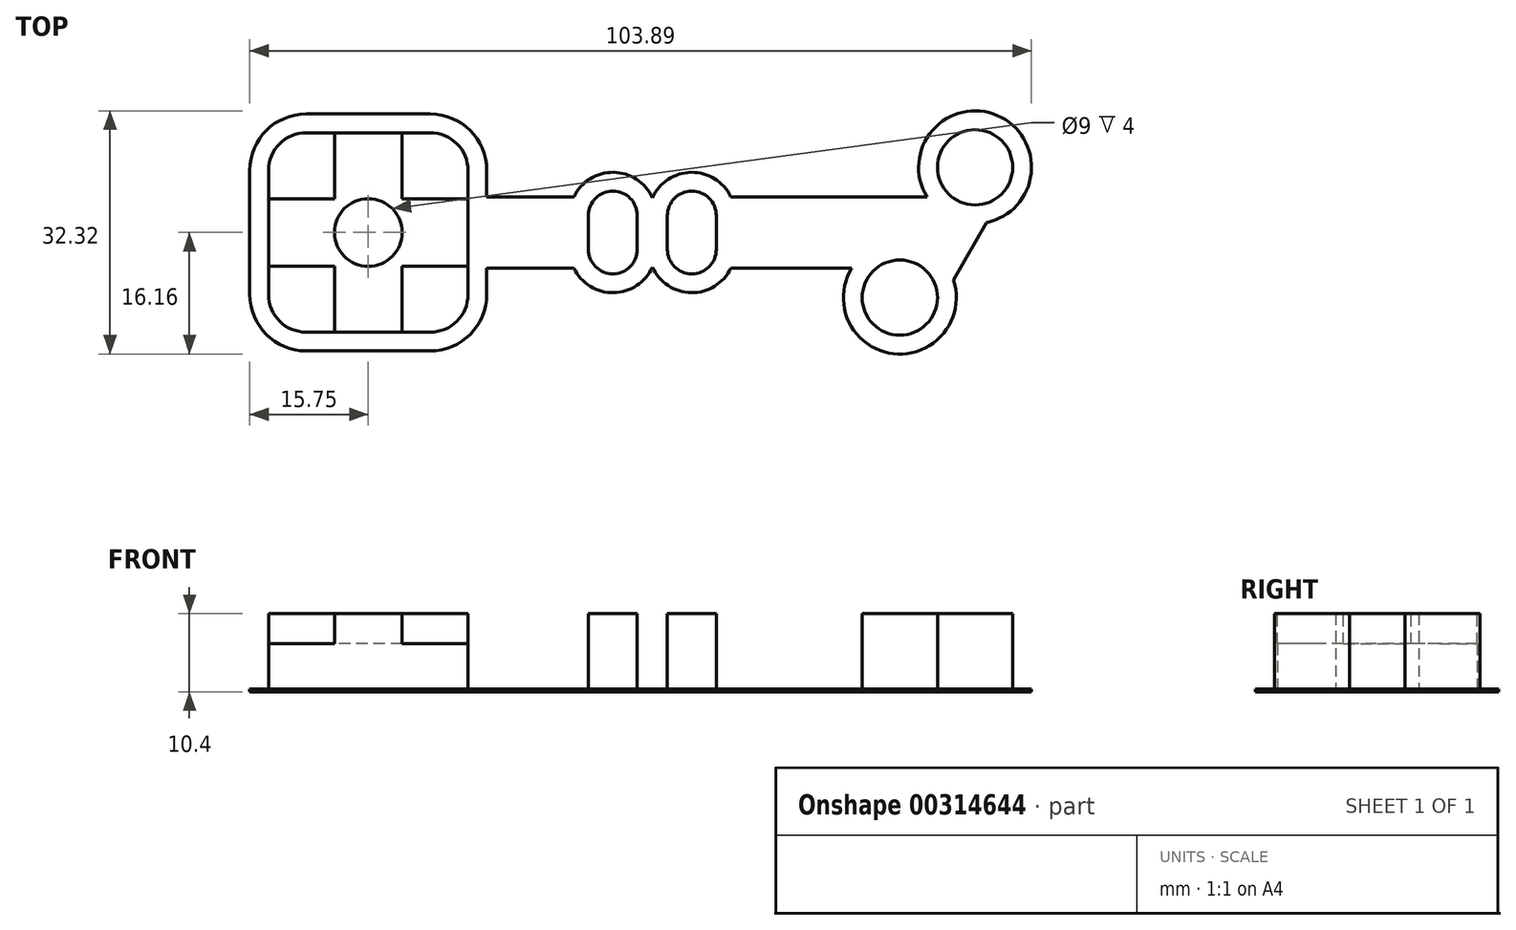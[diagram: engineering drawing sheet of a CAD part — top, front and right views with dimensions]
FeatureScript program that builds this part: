
annotation { "Feature Type Name" : "Feature", "Feature Type Description" : "" }
export const myFeature = defineFeature(function(context is Context, id is Id, definition is map)
    precondition{}
    {
        {
            var Q0;
            Q0=qCreatedBy(makeId("Top.planeOp"),FACE);
            var sketch = newSketch(context, id + "F0", { "sketchPlane" : qUnion([Q0])});
            skLineSegment(sketch, "E0.bottom", {"start": v(-8.25, 13.25) * mm, "end": v(8.25, 13.25) * mm});
            skLineSegment(sketch, "E0.top", {"start": v(-8.25, -13.25) * mm, "end": v(8.25, -13.25) * mm});
            skLineSegment(sketch, "E0.left", {"start": v(-13.25, 8.25) * mm, "end": v(-13.25, -8.25) * mm});
            skLineSegment(sketch, "E0.right", {"start": v(13.25, 8.25) * mm, "end": v(13.25, 2.25) * mm});
            skPoint(sketch, "E0.middle", {"position": v(0, 0) * mm});
            skPoint(sketch, "E1.visualSharp", {"position": v(-13.25, 13.25) * mm});
            skArc(sketch, "E1.filletArc", {"start": v(-8.25, 13.25) * mm, "mid": v(-11.79, 11.79) * mm, "end": v(-13.25, 8.25) * mm});
            skPoint(sketch, "E2.visualSharp", {"position": v(13.25, 13.25) * mm});
            skArc(sketch, "E2.filletArc", {"start": v(13.25, 8.25) * mm, "mid": v(11.79, 11.79) * mm, "end": v(8.25, 13.25) * mm});
            skPoint(sketch, "E3.visualSharp", {"position": v(13.25, -13.25) * mm});
            skArc(sketch, "E3.filletArc", {"start": v(8.25, -13.25) * mm, "mid": v(11.79, -11.79) * mm, "end": v(13.25, -8.25) * mm});
            skPoint(sketch, "E4.visualSharp", {"position": v(-13.25, -13.25) * mm});
            skArc(sketch, "E4.filletArc", {"start": v(-13.25, -8.25) * mm, "mid": v(-11.79, -11.79) * mm, "end": v(-8.25, -13.25) * mm});
            skCircle(sketch, "E5", {"center": v(0, 0) * mm, "radius": 4.5 * mm});
            skLineSegment(sketch, "E6", {"start": v(-4.5, 13.25) * mm, "end": v(-4.5, -13.25) * mm});
            skLineSegment(sketch, "E7", {"start": v(4.5, 13.25) * mm, "end": v(4.5, -13.25) * mm});
            skLineSegment(sketch, "E8", {"start": v(-13.25, 4.5) * mm, "end": v(13.25, 4.5) * mm});
            skLineSegment(sketch, "E9", {"start": v(-13.25, -4.5) * mm, "end": v(13.25, -4.5) * mm});
            skLineSegment(sketch, "E10", {"start": v(-52.76, 0) * mm, "end": v(91.1, 0) * mm, "construction": true});
            skLineSegment(sketch, "E11", {"start": v(13.25, 2.25) * mm, "end": v(29.25, 2.25) * mm});
            skLineSegment(sketch, "E12.bottom", {"start": v(29.25, 2.25) * mm, "end": v(35.75, 2.25) * mm});
            skLineSegment(sketch, "E12.top", {"start": v(29.25, -2.25) * mm, "end": v(35.75, -2.25) * mm});
            skLineSegment(sketch, "E12.left", {"start": v(29.25, 2.25) * mm, "end": v(29.25, -2.25) * mm});
            skLineSegment(sketch, "E12.right", {"start": v(35.75, 2.25) * mm, "end": v(35.75, -2.25) * mm});
            skLineSegment(sketch, "E13", {"start": v(37.75, 18.47) * mm, "end": v(37.75, -25.73) * mm, "construction": true});
            skLineSegment(sketch, "E14.MirrorCS", {"start": v(13.25, -2.25) * mm, "end": v(29.25, -2.25) * mm});
            skLineSegment(sketch, "E15.MirrorCS", {"start": v(46.25, 2.25) * mm, "end": v(46.25, -2.25) * mm});
            skLineSegment(sketch, "E16.MirrorCS", {"start": v(39.75, 2.25) * mm, "end": v(39.75, -2.25) * mm});
            skLineSegment(sketch, "E17.MirrorCS", {"start": v(46.25, -2.25) * mm, "end": v(39.75, -2.25) * mm});
            skLineSegment(sketch, "E18.MirrorCS", {"start": v(46.25, 2.25) * mm, "end": v(39.75, 2.25) * mm});
            skLineSegment(sketch, "E19", {"start": v(35.75, 2.25) * mm, "end": v(39.75, 2.25) * mm});
            skLineSegment(sketch, "E20", {"start": v(35.75, -2.25) * mm, "end": v(39.75, -2.25) * mm});
            skArc(sketch, "E21", {"start": v(29.25, 2.25) * mm, "mid": v(32.5, 5.5) * mm, "end": v(35.75, 2.25) * mm});
            skArc(sketch, "E22.MirrorCS", {"start": v(29.25, -2.25) * mm, "mid": v(32.5, -5.5) * mm, "end": v(35.75, -2.25) * mm});
            skArc(sketch, "E23.MirrorCS", {"start": v(46.25, 2.25) * mm, "mid": v(43, 5.5) * mm, "end": v(39.75, 2.25) * mm});
            skArc(sketch, "E24.MirrorCS", {"start": v(46.25, -2.25) * mm, "mid": v(43, -5.5) * mm, "end": v(39.75, -2.25) * mm});
            skLineSegment(sketch, "E25", {"start": v(46.25, 2.25) * mm, "end": v(74.05, 2.25) * mm});
            skLineSegment(sketch, "E26", {"start": v(80.64, 8.66) * mm, "end": v(70.64, -8.66) * mm, "construction": true});
            skPoint(sketch, "E27", {"position": v(75.64, 0) * mm});
            skLineSegment(sketch, "E28", {"start": v(76.3, 6.16) * mm, "end": v(76.3, 6.16) * mm});
            skLineSegment(sketch, "E29.MirrorCS", {"start": v(80.64, 3.66) * mm, "end": v(74.97, -6.16) * mm});
            skPoint(sketch, "E30", {"position": v(72.75, 0) * mm});
            skLineSegment(sketch, "E31.MirrorCS", {"start": v(46.25, -2.25) * mm, "end": v(71.45, -2.25) * mm});
            skLineSegment(sketch, "E32", {"start": v(13.25, 2.25) * mm, "end": v(13.25, -2.25) * mm});
            skLineSegment(sketch, "E33", {"start": v(13.25, -2.25) * mm, "end": v(13.25, -8.25) * mm});
            skLineSegment(sketch, "E34", {"start": v(74.05, 2.25) * mm, "end": v(74.05, 2.25) * mm});
            skLineSegment(sketch, "E35", {"start": v(71.45, -2.25) * mm, "end": v(71.45, -2.25) * mm});
            skLineSegment(sketch, "E36", {"start": v(71.45, -2.25) * mm, "end": v(70.64, -3.66) * mm});
            skLineSegment(sketch, "E37", {"start": v(74.05, 2.25) * mm, "end": v(71.45, -2.25) * mm});
            skArc(sketch, "E38", {"start": v(70.64, -3.66) * mm, "mid": v(68.14, -13) * mm, "end": v(74.97, -6.16) * mm});
            skArc(sketch, "E39", {"start": v(74.97, -6.16) * mm, "mid": v(73.14, -4.33) * mm, "end": v(70.64, -3.66) * mm});
            skLineSegment(sketch, "E40", {"start": v(76.3, 6.16) * mm, "end": v(74.05, 2.25) * mm});
            skArc(sketch, "E41", {"start": v(80.64, 3.66) * mm, "mid": v(83.14, 13) * mm, "end": v(76.3, 6.16) * mm});
            skArc(sketch, "E42", {"start": v(76.3, 6.16) * mm, "mid": v(78.14, 4.33) * mm, "end": v(80.64, 3.66) * mm});
            skLineSegment(sketch, "E43.0", {"start": v(15.75, 8.25) * mm, "end": v(15.75, 4.75) * mm});
            skLineSegment(sketch, "E43.1", {"start": v(15.75, 4.75) * mm, "end": v(27.32, 4.75) * mm});
            skArc(sketch, "E43.2", {"start": v(27.32, 4.75) * mm, "mid": v(32.59, 8) * mm, "end": v(37.75, 4.6) * mm});
            skArc(sketch, "E43.3", {"start": v(48.18, 4.75) * mm, "mid": v(42.91, 8) * mm, "end": v(37.75, 4.6) * mm});
            skLineSegment(sketch, "E43.4", {"start": v(48.18, 4.75) * mm, "end": v(74.24, 4.75) * mm});
            skArc(sketch, "E43.5", {"start": v(15.75, 8.25) * mm, "mid": v(13.55, 13.55) * mm, "end": v(8.25, 15.75) * mm});
            skArc(sketch, "E43.6", {"start": v(82.17, 1.32) * mm, "mid": v(83.61, 15.54) * mm, "end": v(74.24, 4.75) * mm});
            skLineSegment(sketch, "E43.7", {"start": v(82.17, 1.32) * mm, "end": v(77.76, -6.32) * mm});
            skArc(sketch, "E43.8", {"start": v(64.24, -4.75) * mm, "mid": v(69.77, -16.11) * mm, "end": v(77.76, -6.32) * mm});
            skLineSegment(sketch, "E43.9", {"start": v(48.18, -4.75) * mm, "end": v(64.24, -4.75) * mm});
            skArc(sketch, "E43.10", {"start": v(-15.75, -8.25) * mm, "mid": v(-13.55, -13.55) * mm, "end": v(-8.25, -15.75) * mm});
            skLineSegment(sketch, "E43.11", {"start": v(-15.75, 8.25) * mm, "end": v(-15.75, -8.25) * mm});
            skArc(sketch, "E43.12", {"start": v(-8.25, 15.75) * mm, "mid": v(-13.55, 13.55) * mm, "end": v(-15.75, 8.25) * mm});
            skLineSegment(sketch, "E43.13", {"start": v(-8.25, 15.75) * mm, "end": v(8.25, 15.75) * mm});
            skLineSegment(sketch, "E43.14", {"start": v(-8.25, -15.75) * mm, "end": v(8.25, -15.75) * mm});
            skArc(sketch, "E43.15", {"start": v(8.25, -15.75) * mm, "mid": v(13.55, -13.55) * mm, "end": v(15.75, -8.25) * mm});
            skLineSegment(sketch, "E43.16", {"start": v(15.75, -4.75) * mm, "end": v(15.75, -8.25) * mm});
            skLineSegment(sketch, "E43.17", {"start": v(15.75, -4.75) * mm, "end": v(27.32, -4.75) * mm});
            skArc(sketch, "E43.18", {"start": v(27.32, -4.75) * mm, "mid": v(32.59, -8) * mm, "end": v(37.75, -4.6) * mm});
            skArc(sketch, "E43.19", {"start": v(48.18, -4.75) * mm, "mid": v(42.91, -8) * mm, "end": v(37.75, -4.6) * mm});
            skPoint(sketch, "E44", {"position": v(80.64, 3.66) * mm});
            skSolve(sketch);
        }
        {
            var Q0;
            {var subQ5=sQuery(id+"F0.wireOp",EDGE,"E4.filletArc");Q0=makeQuery(id+"F0.imprint","IMPRINT",FACE,{"disambiguationData":[TD([[makeQuery(id+"F0.imprint","IMPRINT",EDGE,{"derivedFrom":subQ5}),1.0]])]});}
            var Q1;
            {var subQ8=sQuery(id+"F0.wireOp",EDGE,"E32");Q1=makeQuery(id+"F0.imprint","IMPRINT",FACE,{"disambiguationData":[TD([[makeQuery(id+"F0.imprint","IMPRINT",EDGE,{"derivedFrom":subQ8}),-1.0]])]});}
            var Q2;
            {var subQ5=sQuery(id+"F0.wireOp",EDGE,"E3.filletArc");Q2=makeQuery(id+"F0.imprint","IMPRINT",FACE,{"disambiguationData":[TD([[makeQuery(id+"F0.imprint","IMPRINT",EDGE,{"derivedFrom":subQ5}),1.0]])]});}
            var Q3;
            Q3=makeQuery(id+"F0.imprint","IMPRINT",FACE,{"disambiguationData":[TD([[makeQuery(id+"F0.imprint","IMPRINT",EDGE,{"derivedFrom":sQuery(id+"F0.wireOp",EDGE,"E12.bottom")}),1.0]])]});
            var Q4;
            Q4=makeQuery(id+"F0.imprint","IMPRINT",FACE,{"disambiguationData":[TD([[makeQuery(id+"F0.imprint","IMPRINT",EDGE,{"derivedFrom":sQuery(id+"F0.wireOp",EDGE,"E38")}),1.0]])]});
            var Q5;
            {var subQ2=sQuery(id+"F0.wireOp",EDGE,"E42");Q5=makeQuery(id+"F0.imprint","IMPRINT",FACE,{"disambiguationData":[TD([[makeQuery(id+"F0.imprint","IMPRINT",EDGE,{"derivedFrom":subQ2}),1.0]])]});}
            var Q6;
            {var subQ4=sQuery(id+"F0.wireOp",EDGE,"E8");var subQ6=sQuery(id+"F0.wireOp",EDGE,"E0.left");var subQ8=makeQuery(id+"F0.imprint","INTERSECT",VERTEX,{"derivedFrom":[subQ6,subQ4]});Q6=makeQuery(id+"F0.imprint","IMPRINT",FACE,{"disambiguationData":[TD([[makeQuery(id+"F0.imprint","IMPRINT",EDGE,{"disambiguationData":[TD([[subQ8,-1.0]])],"derivedFrom":subQ6}),1.0]])]});}
            var Q7;
            Q7=makeQuery(id+"F0.imprint","IMPRINT",FACE,{"disambiguationData":[TD([[makeQuery(id+"F0.imprint","IMPRINT",EDGE,{"derivedFrom":sQuery(id+"F0.wireOp",EDGE,"E18.MirrorCS")}),-1.0]])]});
            var Q8;
            {var subQ17=sQuery(id+"F0.wireOp",EDGE,"E1.filletArc");Q8=makeQuery(id+"F0.imprint","IMPRINT",FACE,{"disambiguationData":[TD([[makeQuery(id+"F0.imprint","IMPRINT",EDGE,{"derivedFrom":subQ17}),-1.0]])]});}
            var Q9;
            Q9=makeQuery(id+"F0.imprint","IMPRINT",FACE,{"disambiguationData":[TD([[makeQuery(id+"F0.imprint","IMPRINT",EDGE,{"derivedFrom":sQuery(id+"F0.wireOp",EDGE,"E12.bottom")}),-1.0]])]});
            var Q10;
            {var subQ0=sQuery(id+"F0.wireOp",EDGE,"E6");var subQ1=sQuery(id+"F0.wireOp",EDGE,"E5");var subQ2=makeQuery(id+"F0.imprint","INTERSECT",VERTEX,{"derivedFrom":[subQ1,subQ0]});Q10=makeQuery(id+"F0.imprint","IMPRINT",FACE,{"disambiguationData":[TD([[makeQuery(id+"F0.imprint","IMPRINT",EDGE,{"disambiguationData":[TD([[subQ2,-1.0]])],"derivedFrom":subQ1}),-1.0]])]});}
            var Q11;
            {var subQ0=sQuery(id+"F0.wireOp",EDGE,"E8");var subQ1=sQuery(id+"F0.wireOp",EDGE,"E5");var subQ2=makeQuery(id+"F0.imprint","INTERSECT",VERTEX,{"derivedFrom":[subQ1,subQ0]});Q11=makeQuery(id+"F0.imprint","IMPRINT",FACE,{"disambiguationData":[TD([[makeQuery(id+"F0.imprint","IMPRINT",EDGE,{"disambiguationData":[TD([[subQ2,-1.0]])],"derivedFrom":subQ1}),-1.0]])]});}
            var Q12;
            {var subQ5=sQuery(id+"F0.wireOp",EDGE,"E2.filletArc");Q12=makeQuery(id+"F0.imprint","IMPRINT",FACE,{"disambiguationData":[TD([[makeQuery(id+"F0.imprint","IMPRINT",EDGE,{"derivedFrom":subQ5}),1.0]])]});}
            var Q13;
            Q13=makeQuery(id+"F0.imprint","IMPRINT",FACE,{"disambiguationData":[TD([[makeQuery(id+"F0.imprint","IMPRINT",EDGE,{"derivedFrom":sQuery(id+"F0.wireOp",EDGE,"E12.top")}),-1.0]])]});
            var Q14;
            {var subQ0=sQuery(id+"F0.wireOp",EDGE,"E29.MirrorCS");Q14=makeQuery(id+"F0.imprint","IMPRINT",FACE,{"disambiguationData":[TD([[makeQuery(id+"F0.imprint","IMPRINT",EDGE,{"derivedFrom":subQ0}),-1.0]])]});}
            var Q15;
            {var subQ0=sQuery(id+"F0.wireOp",EDGE,"E5");var subQ1=makeQuery(id+"F0.imprint","INTERSECT",VERTEX,{"derivedFrom":[subQ0,sQuery(id+"F0.wireOp",EDGE,"E8")]});Q15=makeQuery(id+"F0.imprint","IMPRINT",FACE,{"disambiguationData":[TD([[makeQuery(id+"F0.imprint","IMPRINT",EDGE,{"disambiguationData":[TD([[subQ1,1.0]])],"derivedFrom":subQ0}),1.0]])]});}
            var Q16;
            Q16=makeQuery(id+"F0.imprint","IMPRINT",FACE,{"disambiguationData":[TD([[makeQuery(id+"F0.imprint","IMPRINT",EDGE,{"derivedFrom":sQuery(id+"F0.wireOp",EDGE,"E12.right")}),1.0]])]});
            var Q17;
            {var subQ1=sQuery(id+"F0.wireOp",EDGE,"E0.top");var subQ5=sQuery(id+"F0.wireOp",EDGE,"E6");var subQ6=makeQuery(id+"F0.imprint","INTERSECT",VERTEX,{"derivedFrom":[subQ1,subQ5]});Q17=makeQuery(id+"F0.imprint","IMPRINT",FACE,{"disambiguationData":[TD([[makeQuery(id+"F0.imprint","IMPRINT",EDGE,{"disambiguationData":[TD([[subQ6,-1.0]])],"derivedFrom":subQ1}),1.0]])]});}
            var Q18;
            Q18=makeQuery(id+"F0.imprint","IMPRINT",FACE,{"disambiguationData":[TD([[makeQuery(id+"F0.imprint","IMPRINT",EDGE,{"derivedFrom":sQuery(id+"F0.wireOp",EDGE,"E15.MirrorCS")}),-1.0]])]});
            var Q19;
            {var subQ2=sQuery(id+"F0.wireOp",EDGE,"E6");var subQ5=sQuery(id+"F0.wireOp",EDGE,"E0.bottom");var subQ8=makeQuery(id+"F0.imprint","INTERSECT",VERTEX,{"derivedFrom":[subQ5,subQ2]});Q19=makeQuery(id+"F0.imprint","IMPRINT",FACE,{"disambiguationData":[TD([[makeQuery(id+"F0.imprint","IMPRINT",EDGE,{"disambiguationData":[TD([[subQ8,-1.0]])],"derivedFrom":subQ5}),-1.0]])]});}
            var Q20;
            Q20=makeQuery(id+"F0.imprint","IMPRINT",FACE,{"disambiguationData":[TD([[makeQuery(id+"F0.imprint","IMPRINT",EDGE,{"derivedFrom":sQuery(id+"F0.wireOp",EDGE,"E15.MirrorCS")}),1.0]])]});
            var Q21;
            {var subQ5=sQuery(id+"F0.wireOp",EDGE,"E1.filletArc");Q21=makeQuery(id+"F0.imprint","IMPRINT",FACE,{"disambiguationData":[TD([[makeQuery(id+"F0.imprint","IMPRINT",EDGE,{"derivedFrom":subQ5}),1.0]])]});}
            var Q22;
            Q22=makeQuery(id+"F0.imprint","IMPRINT",FACE,{"disambiguationData":[TD([[makeQuery(id+"F0.imprint","IMPRINT",EDGE,{"derivedFrom":sQuery(id+"F0.wireOp",EDGE,"E17.MirrorCS")}),1.0]])]});
            var Q23;
            Q23=makeQuery(id+"F0.imprint","IMPRINT",FACE,{"disambiguationData":[TD([[makeQuery(id+"F0.imprint","IMPRINT",EDGE,{"derivedFrom":sQuery(id+"F0.wireOp",EDGE,"E11")}),-1.0]])]});
            var Q24;
            {var subQ0=sQuery(id+"F0.wireOp",EDGE,"E8");var subQ1=sQuery(id+"F0.wireOp",EDGE,"E5");var subQ2=makeQuery(id+"F0.imprint","INTERSECT",VERTEX,{"derivedFrom":[subQ1,subQ0]});Q24=makeQuery(id+"F0.imprint","IMPRINT",FACE,{"disambiguationData":[TD([[makeQuery(id+"F0.imprint","IMPRINT",EDGE,{"disambiguationData":[TD([[subQ2,1.0]])],"derivedFrom":subQ1}),-1.0]])]});}
            var Q25;
            {var subQ0=sQuery(id+"F0.wireOp",EDGE,"E7");var subQ1=sQuery(id+"F0.wireOp",EDGE,"E5");var subQ2=makeQuery(id+"F0.imprint","INTERSECT",VERTEX,{"derivedFrom":[subQ1,subQ0]});Q25=makeQuery(id+"F0.imprint","IMPRINT",FACE,{"disambiguationData":[TD([[makeQuery(id+"F0.imprint","IMPRINT",EDGE,{"disambiguationData":[TD([[subQ2,1.0]])],"derivedFrom":subQ1}),-1.0]])]});}
            extrude(context, id + "F1", {"entities" : qUnion([Q0, Q1, Q2, Q3, Q4, Q5, Q6, Q7, Q8, Q9, Q10, Q11, Q12, Q13, Q14, Q15, Q16, Q17, Q18, Q19, Q20, Q21, Q22, Q23, Q24, Q25]), "depth" : 0.4 * mm});
        }
        {
            var Q0;
            Q0=makeQuery(id+"F1.opExtrude","CAP_FACE",FACE,{"disambiguationData":[OSD([sQuery(id+"F0.wireOp",EDGE,"E43.0"),sQuery(id+"F0.wireOp",EDGE,"E43.1"),sQuery(id+"F0.wireOp",EDGE,"E43.2"),sQuery(id+"F0.wireOp",EDGE,"E43.3"),sQuery(id+"F0.wireOp",EDGE,"E43.4"),sQuery(id+"F0.wireOp",EDGE,"E43.5"),sQuery(id+"F0.wireOp",EDGE,"E43.6"),sQuery(id+"F0.wireOp",EDGE,"E43.7"),sQuery(id+"F0.wireOp",EDGE,"E43.8"),sQuery(id+"F0.wireOp",EDGE,"E43.9"),sQuery(id+"F0.wireOp",EDGE,"E43.10"),sQuery(id+"F0.wireOp",EDGE,"E43.11"),sQuery(id+"F0.wireOp",EDGE,"E43.12"),sQuery(id+"F0.wireOp",EDGE,"E43.13"),sQuery(id+"F0.wireOp",EDGE,"E43.14"),sQuery(id+"F0.wireOp",EDGE,"E43.15"),sQuery(id+"F0.wireOp",EDGE,"E43.16"),sQuery(id+"F0.wireOp",EDGE,"E43.17"),sQuery(id+"F0.wireOp",EDGE,"E43.18"),sQuery(id+"F0.wireOp",EDGE,"E43.19")])],"isStart":false});
            var sketch = newSketch(context, id + "F2", { "sketchPlane" : qUnion([Q0])});
            skLineSegment(sketch, "E45.0", {"start": v(-8.25, 13.25) * mm, "end": v(8.25, 13.25) * mm});
            skLineSegment(sketch, "E45.1", {"start": v(-8.25, -13.25) * mm, "end": v(8.25, -13.25) * mm});
            skLineSegment(sketch, "E45.2", {"start": v(-13.25, 8.25) * mm, "end": v(-13.25, -8.25) * mm});
            skLineSegment(sketch, "E45.3", {"start": v(13.25, 8.25) * mm, "end": v(13.25, 2.25) * mm});
            skPoint(sketch, "E45.4", {"position": v(0, 0) * mm});
            skPoint(sketch, "E45.5", {"position": v(-13.25, 13.25) * mm});
            skArc(sketch, "E45.6", {"start": v(-8.25, 13.25) * mm, "mid": v(-11.79, 11.79) * mm, "end": v(-13.25, 8.25) * mm});
            skPoint(sketch, "E45.7", {"position": v(13.25, 13.25) * mm});
            skArc(sketch, "E45.8", {"start": v(13.25, 8.25) * mm, "mid": v(11.79, 11.79) * mm, "end": v(8.25, 13.25) * mm});
            skPoint(sketch, "E45.9", {"position": v(13.25, -13.25) * mm});
            skArc(sketch, "E45.10", {"start": v(8.25, -13.25) * mm, "mid": v(11.79, -11.79) * mm, "end": v(13.25, -8.25) * mm});
            skPoint(sketch, "E45.11", {"position": v(-13.25, -13.25) * mm});
            skArc(sketch, "E45.12", {"start": v(-13.25, -8.25) * mm, "mid": v(-11.79, -11.79) * mm, "end": v(-8.25, -13.25) * mm});
            skCircle(sketch, "E45.13", {"center": v(0, 0) * mm, "radius": 4.5 * mm});
            skLineSegment(sketch, "E45.14", {"start": v(-4.5, 13.25) * mm, "end": v(-4.5, -13.25) * mm});
            skLineSegment(sketch, "E45.15", {"start": v(4.5, 13.25) * mm, "end": v(4.5, -13.25) * mm});
            skLineSegment(sketch, "E45.16", {"start": v(-13.25, 4.5) * mm, "end": v(13.25, 4.5) * mm});
            skLineSegment(sketch, "E45.17", {"start": v(-13.25, -4.5) * mm, "end": v(13.25, -4.5) * mm});
            skLineSegment(sketch, "E45.19", {"start": v(13.25, 2.25) * mm, "end": v(29.25, 2.25) * mm});
            skLineSegment(sketch, "E45.20", {"start": v(29.25, 2.25) * mm, "end": v(35.75, 2.25) * mm});
            skLineSegment(sketch, "E45.21", {"start": v(29.25, -2.25) * mm, "end": v(35.75, -2.25) * mm});
            skLineSegment(sketch, "E45.22", {"start": v(29.25, 2.25) * mm, "end": v(29.25, -2.25) * mm});
            skLineSegment(sketch, "E45.23", {"start": v(35.75, 2.25) * mm, "end": v(35.75, -2.25) * mm});
            skLineSegment(sketch, "E45.25", {"start": v(13.25, -2.25) * mm, "end": v(29.25, -2.25) * mm});
            skLineSegment(sketch, "E45.26", {"start": v(46.25, 2.25) * mm, "end": v(46.25, -2.25) * mm});
            skLineSegment(sketch, "E45.27", {"start": v(39.75, 2.25) * mm, "end": v(39.75, -2.25) * mm});
            skLineSegment(sketch, "E45.28", {"start": v(46.25, -2.25) * mm, "end": v(39.75, -2.25) * mm});
            skLineSegment(sketch, "E45.29", {"start": v(46.25, 2.25) * mm, "end": v(39.75, 2.25) * mm});
            skLineSegment(sketch, "E45.30", {"start": v(35.75, 2.25) * mm, "end": v(39.75, 2.25) * mm});
            skLineSegment(sketch, "E45.31", {"start": v(35.75, -2.25) * mm, "end": v(39.75, -2.25) * mm});
            skArc(sketch, "E45.32", {"start": v(29.25, 2.25) * mm, "mid": v(32.5, 5.5) * mm, "end": v(35.75, 2.25) * mm});
            skArc(sketch, "E45.33", {"start": v(29.25, -2.25) * mm, "mid": v(32.5, -5.5) * mm, "end": v(35.75, -2.25) * mm});
            skArc(sketch, "E45.34", {"start": v(46.25, 2.25) * mm, "mid": v(43, 5.5) * mm, "end": v(39.75, 2.25) * mm});
            skArc(sketch, "E45.35", {"start": v(46.25, -2.25) * mm, "mid": v(43, -5.5) * mm, "end": v(39.75, -2.25) * mm});
            skLineSegment(sketch, "E45.36", {"start": v(46.25, 2.25) * mm, "end": v(74.05, 2.25) * mm});
            skLineSegment(sketch, "E45.37", {"start": v(80.64, 8.66) * mm, "end": v(70.64, -8.66) * mm});
            skPoint(sketch, "E45.38", {"position": v(75.64, 0) * mm});
            skPoint(sketch, "E45.39", {"position": v(76.3, 6.16) * mm});
            skLineSegment(sketch, "E45.40", {"start": v(80.64, 3.66) * mm, "end": v(74.97, -6.16) * mm});
            skPoint(sketch, "E45.41", {"position": v(72.75, 0) * mm});
            skLineSegment(sketch, "E45.42", {"start": v(46.25, -2.25) * mm, "end": v(71.45, -2.25) * mm});
            skLineSegment(sketch, "E45.43", {"start": v(13.25, 2.25) * mm, "end": v(13.25, -2.25) * mm});
            skLineSegment(sketch, "E45.44", {"start": v(13.25, -2.25) * mm, "end": v(13.25, -8.25) * mm});
            skPoint(sketch, "E45.45", {"position": v(74.05, 2.25) * mm});
            skPoint(sketch, "E45.46", {"position": v(71.45, -2.25) * mm});
            skLineSegment(sketch, "E45.47", {"start": v(71.45, -2.25) * mm, "end": v(70.64, -3.66) * mm});
            skLineSegment(sketch, "E45.48", {"start": v(74.05, 2.25) * mm, "end": v(71.45, -2.25) * mm});
            skArc(sketch, "E45.49", {"start": v(70.64, -3.66) * mm, "mid": v(68.14, -13) * mm, "end": v(74.97, -6.16) * mm});
            skArc(sketch, "E45.50", {"start": v(74.97, -6.16) * mm, "mid": v(73.14, -4.33) * mm, "end": v(70.64, -3.66) * mm});
            skLineSegment(sketch, "E45.51", {"start": v(76.3, 6.16) * mm, "end": v(74.05, 2.25) * mm});
            skArc(sketch, "E45.52", {"start": v(80.64, 3.66) * mm, "mid": v(83.14, 13) * mm, "end": v(76.3, 6.16) * mm});
            skArc(sketch, "E45.53", {"start": v(76.3, 6.16) * mm, "mid": v(78.14, 4.33) * mm, "end": v(80.64, 3.66) * mm});
            skLineSegment(sketch, "E45.54", {"start": v(15.75, 8.25) * mm, "end": v(15.75, 4.75) * mm});
            skLineSegment(sketch, "E45.55", {"start": v(15.75, 4.75) * mm, "end": v(27.32, 4.75) * mm});
            skArc(sketch, "E45.56", {"start": v(27.32, 4.75) * mm, "mid": v(32.59, 8) * mm, "end": v(37.75, 4.6) * mm});
            skArc(sketch, "E45.57", {"start": v(48.18, 4.75) * mm, "mid": v(42.91, 8) * mm, "end": v(37.75, 4.6) * mm});
            skLineSegment(sketch, "E45.58", {"start": v(48.18, 4.75) * mm, "end": v(74.24, 4.75) * mm});
            skArc(sketch, "E45.59", {"start": v(15.75, 8.25) * mm, "mid": v(13.55, 13.55) * mm, "end": v(8.25, 15.75) * mm});
            skArc(sketch, "E45.60", {"start": v(82.17, 1.32) * mm, "mid": v(83.61, 15.54) * mm, "end": v(74.24, 4.75) * mm});
            skLineSegment(sketch, "E45.61", {"start": v(82.17, 1.32) * mm, "end": v(77.76, -6.32) * mm});
            skArc(sketch, "E45.62", {"start": v(64.24, -4.75) * mm, "mid": v(69.77, -16.11) * mm, "end": v(77.76, -6.32) * mm});
            skLineSegment(sketch, "E45.63", {"start": v(48.18, -4.75) * mm, "end": v(64.24, -4.75) * mm});
            skArc(sketch, "E45.64", {"start": v(-15.75, -8.25) * mm, "mid": v(-13.55, -13.55) * mm, "end": v(-8.25, -15.75) * mm});
            skLineSegment(sketch, "E45.65", {"start": v(-15.75, 8.25) * mm, "end": v(-15.75, -8.25) * mm});
            skArc(sketch, "E45.66", {"start": v(-8.25, 15.75) * mm, "mid": v(-13.55, 13.55) * mm, "end": v(-15.75, 8.25) * mm});
            skLineSegment(sketch, "E45.67", {"start": v(-8.25, 15.75) * mm, "end": v(8.25, 15.75) * mm});
            skLineSegment(sketch, "E45.68", {"start": v(-8.25, -15.75) * mm, "end": v(8.25, -15.75) * mm});
            skArc(sketch, "E45.69", {"start": v(8.25, -15.75) * mm, "mid": v(13.55, -13.55) * mm, "end": v(15.75, -8.25) * mm});
            skLineSegment(sketch, "E45.70", {"start": v(15.75, -4.75) * mm, "end": v(15.75, -8.25) * mm});
            skLineSegment(sketch, "E45.71", {"start": v(15.75, -4.75) * mm, "end": v(27.32, -4.75) * mm});
            skArc(sketch, "E45.72", {"start": v(27.32, -4.75) * mm, "mid": v(32.59, -8) * mm, "end": v(37.75, -4.6) * mm});
            skArc(sketch, "E45.73", {"start": v(48.18, -4.75) * mm, "mid": v(42.91, -8) * mm, "end": v(37.75, -4.6) * mm});
            skPoint(sketch, "E45.74", {"position": v(80.64, 3.66) * mm});
            skSolve(sketch);
        }
        {
            var Q0;
            {var subQ4=sQuery(id+"F2.wireOp",EDGE,"E45.16");var subQ6=sQuery(id+"F2.wireOp",EDGE,"E45.2");var subQ8=makeQuery(id+"F2.imprint","INTERSECT",VERTEX,{"derivedFrom":[subQ6,subQ4]});Q0=makeQuery(id+"F2.imprint","IMPRINT",FACE,{"disambiguationData":[TD([[makeQuery(id+"F2.imprint","IMPRINT",EDGE,{"disambiguationData":[TD([[subQ8,-1.0]])],"derivedFrom":subQ6}),1.0]])]});}
            var Q1;
            Q1=makeQuery(id+"F2.imprint","IMPRINT",FACE,{"disambiguationData":[TD([[makeQuery(id+"F2.imprint","IMPRINT",EDGE,{"derivedFrom":sQuery(id+"F2.wireOp",EDGE,"E45.20")}),1.0]])]});
            var Q2;
            Q2=makeQuery(id+"F2.imprint","IMPRINT",FACE,{"disambiguationData":[TD([[makeQuery(id+"F2.imprint","IMPRINT",EDGE,{"derivedFrom":sQuery(id+"F2.wireOp",EDGE,"E45.20")}),-1.0]])]});
            var Q3;
            Q3=makeQuery(id+"F2.imprint","IMPRINT",FACE,{"disambiguationData":[TD([[makeQuery(id+"F2.imprint","IMPRINT",EDGE,{"derivedFrom":sQuery(id+"F2.wireOp",EDGE,"E45.21")}),-1.0]])]});
            var Q4;
            {var subQ5=sQuery(id+"F2.wireOp",EDGE,"E45.12");Q4=makeQuery(id+"F2.imprint","IMPRINT",FACE,{"disambiguationData":[TD([[makeQuery(id+"F2.imprint","IMPRINT",EDGE,{"derivedFrom":subQ5}),1.0]])]});}
            var Q5;
            {var subQ1=sQuery(id+"F2.wireOp",EDGE,"E45.1");var subQ5=sQuery(id+"F2.wireOp",EDGE,"E45.14");var subQ6=makeQuery(id+"F2.imprint","INTERSECT",VERTEX,{"derivedFrom":[subQ1,subQ5]});Q5=makeQuery(id+"F2.imprint","IMPRINT",FACE,{"disambiguationData":[TD([[makeQuery(id+"F2.imprint","IMPRINT",EDGE,{"disambiguationData":[TD([[subQ6,-1.0]])],"derivedFrom":subQ1}),1.0]])]});}
            var Q6;
            {var subQ7=sQuery(id+"F2.wireOp",EDGE,"E45.10");Q6=makeQuery(id+"F2.imprint","IMPRINT",FACE,{"disambiguationData":[TD([[makeQuery(id+"F2.imprint","IMPRINT",EDGE,{"derivedFrom":subQ7}),1.0]])]});}
            var Q7;
            {var subQ8=sQuery(id+"F2.wireOp",EDGE,"E45.43");Q7=makeQuery(id+"F2.imprint","IMPRINT",FACE,{"disambiguationData":[TD([[makeQuery(id+"F2.imprint","IMPRINT",EDGE,{"derivedFrom":subQ8}),-1.0]])]});}
            var Q8;
            {var subQ0=sQuery(id+"F2.wireOp",EDGE,"E45.13");var subQ1=makeQuery(id+"F2.imprint","INTERSECT",VERTEX,{"derivedFrom":[subQ0,sQuery(id+"F2.wireOp",EDGE,"E45.16")]});Q8=makeQuery(id+"F2.imprint","IMPRINT",FACE,{"disambiguationData":[TD([[makeQuery(id+"F2.imprint","IMPRINT",EDGE,{"disambiguationData":[TD([[subQ1,1.0]])],"derivedFrom":subQ0}),1.0]])]});}
            var Q9;
            {var subQ0=sQuery(id+"F2.wireOp",EDGE,"E45.15");var subQ1=sQuery(id+"F2.wireOp",EDGE,"E45.13");var subQ2=makeQuery(id+"F2.imprint","INTERSECT",VERTEX,{"derivedFrom":[subQ1,subQ0]});Q9=makeQuery(id+"F2.imprint","IMPRINT",FACE,{"disambiguationData":[TD([[makeQuery(id+"F2.imprint","IMPRINT",EDGE,{"disambiguationData":[TD([[subQ2,1.0]])],"derivedFrom":subQ1}),-1.0]])]});}
            var Q10;
            {var subQ0=sQuery(id+"F2.wireOp",EDGE,"E45.14");var subQ1=sQuery(id+"F2.wireOp",EDGE,"E45.13");var subQ2=makeQuery(id+"F2.imprint","INTERSECT",VERTEX,{"derivedFrom":[subQ1,subQ0]});Q10=makeQuery(id+"F2.imprint","IMPRINT",FACE,{"disambiguationData":[TD([[makeQuery(id+"F2.imprint","IMPRINT",EDGE,{"disambiguationData":[TD([[subQ2,-1.0]])],"derivedFrom":subQ1}),-1.0]])]});}
            var Q11;
            {var subQ0=sQuery(id+"F2.wireOp",EDGE,"E45.16");var subQ1=sQuery(id+"F2.wireOp",EDGE,"E45.13");var subQ2=makeQuery(id+"F2.imprint","INTERSECT",VERTEX,{"derivedFrom":[subQ1,subQ0]});Q11=makeQuery(id+"F2.imprint","IMPRINT",FACE,{"disambiguationData":[TD([[makeQuery(id+"F2.imprint","IMPRINT",EDGE,{"disambiguationData":[TD([[subQ2,-1.0]])],"derivedFrom":subQ1}),-1.0]])]});}
            var Q12;
            {var subQ2=sQuery(id+"F2.wireOp",EDGE,"E45.14");var subQ5=sQuery(id+"F2.wireOp",EDGE,"E45.0");var subQ8=makeQuery(id+"F2.imprint","INTERSECT",VERTEX,{"derivedFrom":[subQ5,subQ2]});Q12=makeQuery(id+"F2.imprint","IMPRINT",FACE,{"disambiguationData":[TD([[makeQuery(id+"F2.imprint","IMPRINT",EDGE,{"disambiguationData":[TD([[subQ8,-1.0]])],"derivedFrom":subQ5}),-1.0]])]});}
            var Q13;
            {var subQ5=sQuery(id+"F2.wireOp",EDGE,"E45.6");Q13=makeQuery(id+"F2.imprint","IMPRINT",FACE,{"disambiguationData":[TD([[makeQuery(id+"F2.imprint","IMPRINT",EDGE,{"derivedFrom":subQ5}),1.0]])]});}
            var Q14;
            {var subQ5=sQuery(id+"F2.wireOp",EDGE,"E45.8");Q14=makeQuery(id+"F2.imprint","IMPRINT",FACE,{"disambiguationData":[TD([[makeQuery(id+"F2.imprint","IMPRINT",EDGE,{"derivedFrom":subQ5}),1.0]])]});}
            var Q15;
            {var subQ0=sQuery(id+"F2.wireOp",EDGE,"E45.16");var subQ1=sQuery(id+"F2.wireOp",EDGE,"E45.13");var subQ2=makeQuery(id+"F2.imprint","INTERSECT",VERTEX,{"derivedFrom":[subQ1,subQ0]});Q15=makeQuery(id+"F2.imprint","IMPRINT",FACE,{"disambiguationData":[TD([[makeQuery(id+"F2.imprint","IMPRINT",EDGE,{"disambiguationData":[TD([[subQ2,1.0]])],"derivedFrom":subQ1}),-1.0]])]});}
            var Q16;
            Q16=makeQuery(id+"F2.imprint","IMPRINT",FACE,{"disambiguationData":[TD([[makeQuery(id+"F2.imprint","IMPRINT",EDGE,{"derivedFrom":sQuery(id+"F2.wireOp",EDGE,"E45.26")}),-1.0]])]});
            var Q17;
            Q17=makeQuery(id+"F2.imprint","IMPRINT",FACE,{"disambiguationData":[TD([[makeQuery(id+"F2.imprint","IMPRINT",EDGE,{"derivedFrom":sQuery(id+"F2.wireOp",EDGE,"E45.29")}),-1.0]])]});
            var Q18;
            Q18=makeQuery(id+"F2.imprint","IMPRINT",FACE,{"disambiguationData":[TD([[makeQuery(id+"F2.imprint","IMPRINT",EDGE,{"derivedFrom":sQuery(id+"F2.wireOp",EDGE,"E45.28")}),1.0]])]});
            var Q19;
            {var subQ0=sQuery(id+"F2.wireOp",EDGE,"E45.49");Q19=makeQuery(id+"F2.imprint","IMPRINT",FACE,{"disambiguationData":[TD([[makeQuery(id+"F2.imprint","IMPRINT",EDGE,{"derivedFrom":subQ0}),1.0]])]});}
            var Q20;
            {var subQ0=sQuery(id+"F2.wireOp",EDGE,"E45.52");var subQ1=makeQuery(id+"F2.imprint","INTERSECT",VERTEX,{"derivedFrom":[sQuery(id+"F2.wireOp",EDGE,"E45.40"),subQ0]});Q20=makeQuery(id+"F2.imprint","IMPRINT",FACE,{"disambiguationData":[TD([[makeQuery(id+"F2.imprint","IMPRINT",EDGE,{"disambiguationData":[TD([[subQ1,1.0]])],"derivedFrom":subQ0}),1.0]])]});}
            extrude(context, id + "F3", {"entities" : qUnion([Q0, Q1, Q2, Q3, Q4, Q5, Q6, Q7, Q8, Q9, Q10, Q11, Q12, Q13, Q14, Q15, Q16, Q17, Q18, Q19, Q20]), "operationType" : NewBodyOperationType.ADD, "depth" : 10 * mm});
        }
        {
            var Q0;
            Q0=makeQuery(id+"F3.opExtrude","CAP_FACE",FACE,{"disambiguationData":[OSD([sQuery(id+"F2.wireOp",EDGE,"E45.0"),sQuery(id+"F2.wireOp",EDGE,"E45.1"),sQuery(id+"F2.wireOp",EDGE,"E45.2"),sQuery(id+"F2.wireOp",EDGE,"E45.3"),sQuery(id+"F2.wireOp",EDGE,"E45.6"),sQuery(id+"F2.wireOp",EDGE,"E45.8"),sQuery(id+"F2.wireOp",EDGE,"E45.10"),sQuery(id+"F2.wireOp",EDGE,"E45.12"),sQuery(id+"F2.wireOp",EDGE,"E45.43"),sQuery(id+"F2.wireOp",EDGE,"E45.44")])],"isStart":false});
            var sketch = newSketch(context, id + "F4", { "sketchPlane" : qUnion([Q0])});
            skLineSegment(sketch, "E46.0", {"start": v(-8.25, 13.25) * mm, "end": v(8.25, 13.25) * mm});
            skLineSegment(sketch, "E46.1", {"start": v(-8.25, -13.25) * mm, "end": v(8.25, -13.25) * mm});
            skLineSegment(sketch, "E46.2", {"start": v(-13.25, 8.25) * mm, "end": v(-13.25, -8.25) * mm});
            skLineSegment(sketch, "E46.3", {"start": v(13.25, 8.25) * mm, "end": v(13.25, 2.25) * mm});
            skPoint(sketch, "E46.4", {"position": v(0, 0) * mm});
            skPoint(sketch, "E46.5", {"position": v(-13.25, 13.25) * mm});
            skArc(sketch, "E46.6", {"start": v(-8.25, 13.25) * mm, "mid": v(-11.79, 11.79) * mm, "end": v(-13.25, 8.25) * mm});
            skPoint(sketch, "E46.7", {"position": v(13.25, 13.25) * mm});
            skArc(sketch, "E46.8", {"start": v(13.25, 8.25) * mm, "mid": v(11.79, 11.79) * mm, "end": v(8.25, 13.25) * mm});
            skPoint(sketch, "E46.9", {"position": v(13.25, -13.25) * mm});
            skArc(sketch, "E46.10", {"start": v(8.25, -13.25) * mm, "mid": v(11.79, -11.79) * mm, "end": v(13.25, -8.25) * mm});
            skPoint(sketch, "E46.11", {"position": v(-13.25, -13.25) * mm});
            skArc(sketch, "E46.12", {"start": v(-13.25, -8.25) * mm, "mid": v(-11.79, -11.79) * mm, "end": v(-8.25, -13.25) * mm});
            skCircle(sketch, "E46.13", {"center": v(0, 0) * mm, "radius": 4.5 * mm});
            skLineSegment(sketch, "E46.14", {"start": v(-4.5, 13.25) * mm, "end": v(-4.5, -13.25) * mm});
            skLineSegment(sketch, "E46.15", {"start": v(4.5, 13.25) * mm, "end": v(4.5, -13.25) * mm});
            skLineSegment(sketch, "E46.16", {"start": v(-13.25, 4.5) * mm, "end": v(13.25, 4.5) * mm});
            skLineSegment(sketch, "E46.17", {"start": v(-13.25, -4.5) * mm, "end": v(13.25, -4.5) * mm});
            skLineSegment(sketch, "E46.43", {"start": v(13.25, 2.25) * mm, "end": v(13.25, -2.25) * mm});
            skLineSegment(sketch, "E46.44", {"start": v(13.25, -2.25) * mm, "end": v(13.25, -8.25) * mm});
            skLineSegment(sketch, "E46.54", {"start": v(15.75, 8.25) * mm, "end": v(15.75, 4.75) * mm});
            skArc(sketch, "E46.59", {"start": v(15.75, 8.25) * mm, "mid": v(13.55, 13.55) * mm, "end": v(8.25, 15.75) * mm});
            skArc(sketch, "E46.64", {"start": v(-15.75, -8.25) * mm, "mid": v(-13.55, -13.55) * mm, "end": v(-8.25, -15.75) * mm});
            skLineSegment(sketch, "E46.65", {"start": v(-15.75, 8.25) * mm, "end": v(-15.75, -8.25) * mm});
            skArc(sketch, "E46.66", {"start": v(-8.25, 15.75) * mm, "mid": v(-13.55, 13.55) * mm, "end": v(-15.75, 8.25) * mm});
            skLineSegment(sketch, "E46.67", {"start": v(-8.25, 15.75) * mm, "end": v(8.25, 15.75) * mm});
            skLineSegment(sketch, "E46.68", {"start": v(-8.25, -15.75) * mm, "end": v(8.25, -15.75) * mm});
            skArc(sketch, "E46.69", {"start": v(8.25, -15.75) * mm, "mid": v(13.55, -13.55) * mm, "end": v(15.75, -8.25) * mm});
            skLineSegment(sketch, "E46.70", {"start": v(15.75, -4.75) * mm, "end": v(15.75, -8.25) * mm});
            skSolve(sketch);
        }
        {
            var Q0;
            {var subQ7=sQuery(id+"F4.wireOp",EDGE,"E46.10");Q0=makeQuery(id+"F4.imprint","IMPRINT",FACE,{"disambiguationData":[TD([[makeQuery(id+"F4.imprint","IMPRINT",EDGE,{"derivedFrom":subQ7}),1.0]])]});}
            var Q1;
            {var subQ5=sQuery(id+"F4.wireOp",EDGE,"E46.12");Q1=makeQuery(id+"F4.imprint","IMPRINT",FACE,{"disambiguationData":[TD([[makeQuery(id+"F4.imprint","IMPRINT",EDGE,{"derivedFrom":subQ5}),1.0]])]});}
            var Q2;
            {var subQ5=sQuery(id+"F4.wireOp",EDGE,"E46.6");Q2=makeQuery(id+"F4.imprint","IMPRINT",FACE,{"disambiguationData":[TD([[makeQuery(id+"F4.imprint","IMPRINT",EDGE,{"derivedFrom":subQ5}),1.0]])]});}
            var Q3;
            {var subQ5=sQuery(id+"F4.wireOp",EDGE,"E46.8");Q3=makeQuery(id+"F4.imprint","IMPRINT",FACE,{"disambiguationData":[TD([[makeQuery(id+"F4.imprint","IMPRINT",EDGE,{"derivedFrom":subQ5}),1.0]])]});}
            var Q4;
            {var subQ0=sQuery(id+"F4.wireOp",EDGE,"E46.13");var subQ1=makeQuery(id+"F4.imprint","INTERSECT",VERTEX,{"derivedFrom":[subQ0,sQuery(id+"F4.wireOp",EDGE,"E46.16")]});Q4=makeQuery(id+"F4.imprint","IMPRINT",FACE,{"disambiguationData":[TD([[makeQuery(id+"F4.imprint","IMPRINT",EDGE,{"disambiguationData":[TD([[subQ1,1.0]])],"derivedFrom":subQ0}),1.0]])]});}
            extrude(context, id + "F5", {"entities" : qUnion([Q0, Q1, Q2, Q3, Q4]), "operationType" : NewBodyOperationType.REMOVE, "oppositeDirection" : true, "depth" : 4 * mm});
        }
    });
